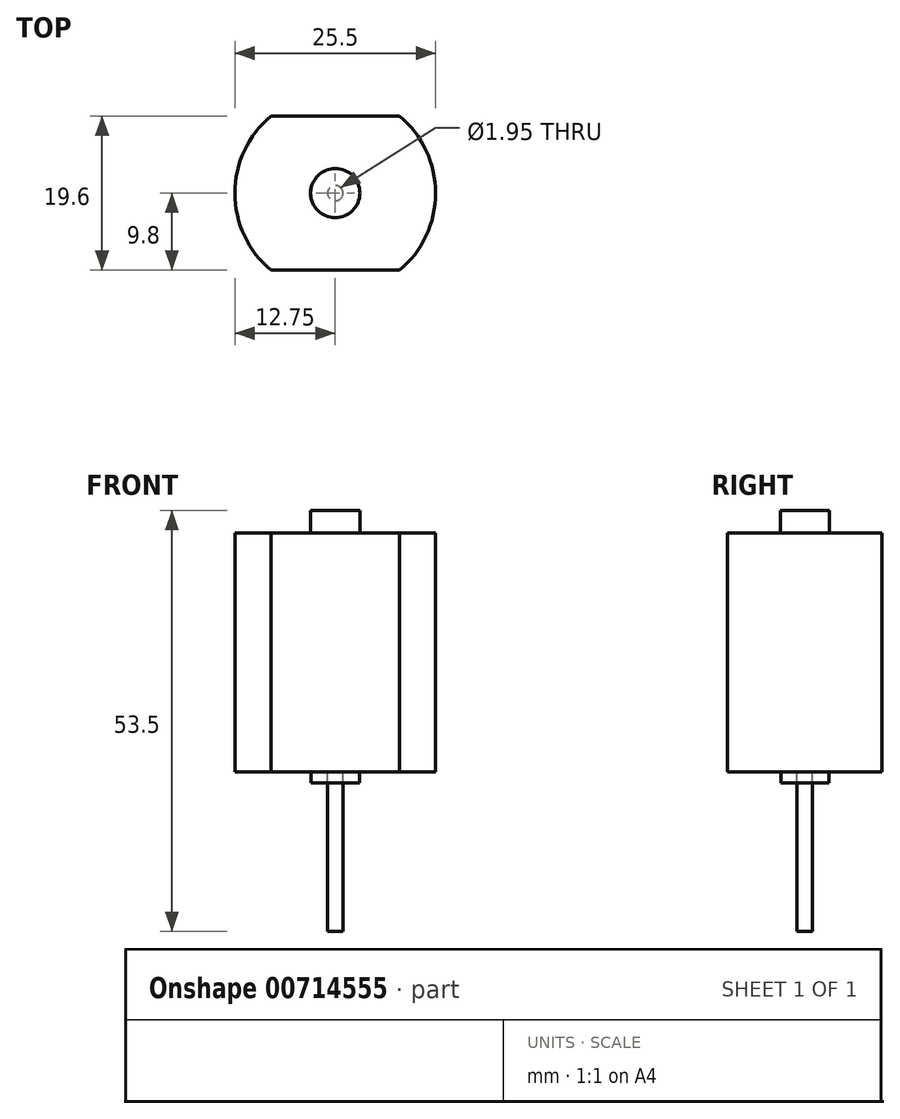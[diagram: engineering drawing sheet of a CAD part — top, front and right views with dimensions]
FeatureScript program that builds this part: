
annotation { "Feature Type Name" : "Feature", "Feature Type Description" : "" }
export const myFeature = defineFeature(function(context is Context, id is Id, definition is map)
    precondition{}
    {
        {
            var Q0;
            Q0=qCreatedBy(makeId("Top.planeOp"),FACE);
            var sketch = newSketch(context, id + "F0", { "sketchPlane" : qUnion([Q0])});
            skCircle(sketch, "E0", {"center": v(0, 0) * mm, "radius": 12.75 * mm});
            skLineSegment(sketch, "E1", {"start": v(-8.16, 9.8) * mm, "end": v(8.16, 9.8) * mm});
            skLineSegment(sketch, "E2", {"start": v(-8.16, -9.8) * mm, "end": v(8.16, -9.8) * mm});
            skLineSegment(sketch, "E3", {"start": v(0, 9.8) * mm, "end": v(0, -9.8) * mm, "construction": true});
            skSolve(sketch);
        }
        {
            var Q0;
            {var subQ0=sQuery(id+"F0.wireOp",EDGE,"E1");Q0=makeQuery(id+"F0.imprint","IMPRINT",FACE,{"disambiguationData":[TD([[makeQuery(id+"F0.imprint","IMPRINT",EDGE,{"derivedFrom":subQ0}),-1.0]])]});}
            extrude(context, id + "F1", {"entities" : qUnion([Q0]), "depth" : 30.35 * mm, "offsetDistance" : 25 * mm});
        }
        {
            var Q0;
            Q0=makeQuery(id+"F1.opExtrude","CAP_FACE",FACE,{"disambiguationData":[OSD([sQuery(id+"F0.wireOp",EDGE,"E0"),sQuery(id+"F0.wireOp",EDGE,"E1"),sQuery(id+"F0.wireOp",EDGE,"E2")])],"isStart":true});
            var sketch = newSketch(context, id + "F2", { "sketchPlane" : qUnion([Q0])});
            skCircle(sketch, "E4", {"center": v(0, 0) * mm, "radius": 3.05 * mm});
            skCircle(sketch, "E5", {"center": v(0, 0) * mm, "radius": 0.97 * mm});
            skSolve(sketch);
        }
        {
            var Q0;
            Q0=makeQuery(id+"F2.imprint","IMPRINT",FACE,{"disambiguationData":[TD([[makeQuery(id+"F2.imprint","IMPRINT",EDGE,{"derivedFrom":sQuery(id+"F2.wireOp",EDGE,"E4")}),1.0]])]});
            extrude(context, id + "F3", {"entities" : qUnion([Q0]), "depth" : 1.4 * mm, "offsetDistance" : 25 * mm});
        }
        {
            var Q0;
            Q0=makeQuery(id+"F1.opExtrude","CAP_FACE",FACE,{"disambiguationData":[OSD([sQuery(id+"F0.wireOp",EDGE,"E0"),sQuery(id+"F0.wireOp",EDGE,"E1"),sQuery(id+"F0.wireOp",EDGE,"E2")])],"isStart":false});
            var sketch = newSketch(context, id + "F4", { "sketchPlane" : qUnion([Q0])});
            skPoint(sketch, "E6.0", {"position": v(0, 0) * mm});
            skCircle(sketch, "E7", {"center": v(0, 0) * mm, "radius": 3.12 * mm});
            skSolve(sketch);
        }
        {
            var Q0;
            Q0=makeQuery(id+"F4.imprint","IMPRINT",FACE,{"disambiguationData":[TD([[makeQuery(id+"F4.imprint","IMPRINT",EDGE,{"derivedFrom":sQuery(id+"F4.wireOp",EDGE,"E7")}),1.0]])]});
            extrude(context, id + "F5", {"entities" : qUnion([Q0]), "depth" : 2.9 * mm, "offsetDistance" : 25 * mm});
        }
        {
            var Q0;
            Q0=makeQuery(id+"F2.imprint","IMPRINT",FACE,{"disambiguationData":[TD([[makeQuery(id+"F2.imprint","IMPRINT",EDGE,{"derivedFrom":sQuery(id+"F2.wireOp",EDGE,"E5")}),1.0]])]});
            extrude(context, id + "F6", {"entities" : qUnion([Q0]), "depth" : 20.25 * mm, "offsetDistance" : 25 * mm});
        }
    });
